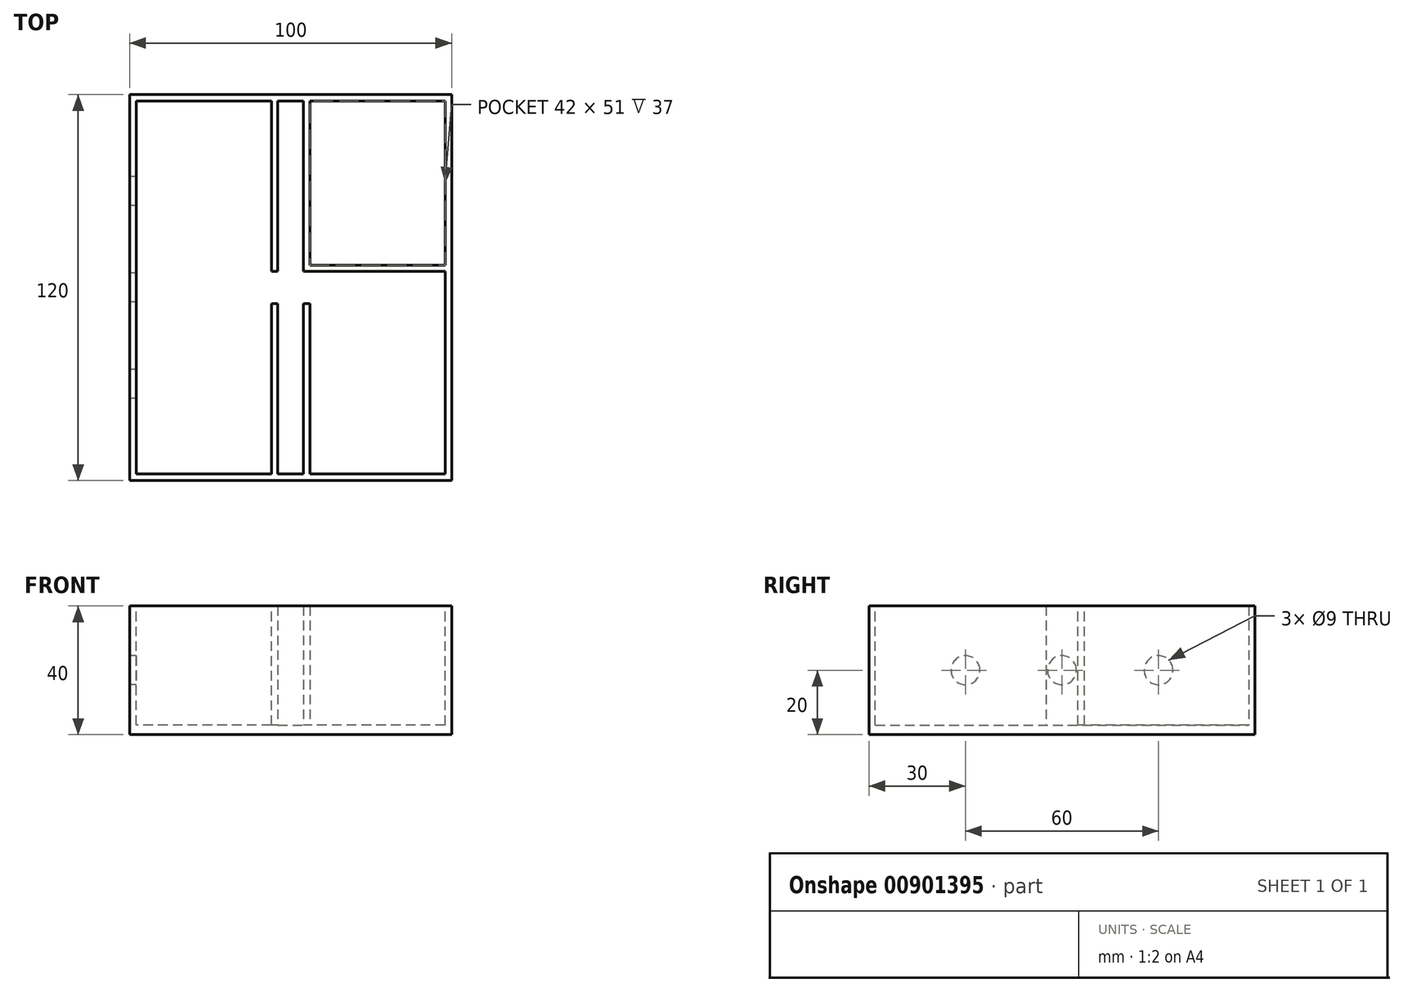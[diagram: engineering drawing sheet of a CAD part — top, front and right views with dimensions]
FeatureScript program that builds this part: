
annotation { "Feature Type Name" : "Feature", "Feature Type Description" : "" }
export const myFeature = defineFeature(function(context is Context, id is Id, definition is map)
    precondition{}
    {
        {
            var Q0;
            Q0=qCreatedBy(makeId("Top.planeOp"),FACE);
            var sketch = newSketch(context, id + "F0", { "sketchPlane" : qUnion([Q0])});
            skLineSegment(sketch, "E0.bottom", {"start": v(50, -60) * mm, "end": v(-50, -60) * mm});
            skLineSegment(sketch, "E0.top", {"start": v(50, 60) * mm, "end": v(-50, 60) * mm});
            skLineSegment(sketch, "E0.left", {"start": v(50, -60) * mm, "end": v(50, 60) * mm});
            skLineSegment(sketch, "E0.right", {"start": v(-50, -60) * mm, "end": v(-50, 60) * mm});
            skPoint(sketch, "E0.middle", {"position": v(0, 0) * mm});
            skSolve(sketch);
        }
        {
            var Q0;
            Q0=makeQuery(id+"F0.imprint","IMPRINT",FACE,{"disambiguationData":[TD([[makeQuery(id+"F0.imprint","IMPRINT",EDGE,{"derivedFrom":sQuery(id+"F0.wireOp",EDGE,"E0.bottom")}),-1.0]])]});
            extrude(context, id + "F1", {"entities" : qUnion([Q0]), "depth" : 40 * mm, "offsetDistance" : 25 * mm});
        }
        {
            var Q0;
            Q0=makeQuery(id+"F1.opExtrude","CAP_FACE",FACE,{"disambiguationData":[OSD([sQuery(id+"F0.wireOp",EDGE,"E0.bottom"),sQuery(id+"F0.wireOp",EDGE,"E0.top"),sQuery(id+"F0.wireOp",EDGE,"E0.left"),sQuery(id+"F0.wireOp",EDGE,"E0.right")])],"isStart":false});
            var sketch = newSketch(context, id + "F2", { "sketchPlane" : qUnion([Q0])});
            skLineSegment(sketch, "E1.bottom", {"start": v(48, -58) * mm, "end": v(-48, -58) * mm});
            skLineSegment(sketch, "E1.top", {"start": v(48, 58) * mm, "end": v(-48, 58) * mm});
            skLineSegment(sketch, "E1.left", {"start": v(48, -58) * mm, "end": v(48, 58) * mm});
            skLineSegment(sketch, "E1.right", {"start": v(-48, -58) * mm, "end": v(-48, 58) * mm});
            skPoint(sketch, "E1.middle", {"position": v(0, 0) * mm});
            skSolve(sketch);
        }
        {
            var Q0;
            Q0 = qSketchRegion(id + "F2", true);
            extrude(context, id + "F3", {"entities" : qUnion([Q0]), "operationType" : NewBodyOperationType.REMOVE, "oppositeDirection" : true, "depth" : 37 * mm, "offsetDistance" : 25 * mm});
        }
        {
            var Q0;
            Q0=makeQuery(id+"F1.opExtrude","SWEPT_FACE",FACE,{"disambiguationData":[OSD([sQuery(id+"F0.wireOp",EDGE,"E0.right")])]});
            var sketch = newSketch(context, id + "F4", { "sketchPlane" : qUnion([Q0])});
            skLineSegment(sketch, "E2", {"start": v(-60, 40) * mm, "end": v(60, 0) * mm, "construction": true});
            skLineSegment(sketch, "E3", {"start": v(60, 40) * mm, "end": v(-60, 0) * mm, "construction": true});
            skCircle(sketch, "E4", {"center": v(0, 20) * mm, "radius": 4.5 * mm});
            skLineSegment(sketch, "E5", {"start": v(0, 40) * mm, "end": v(-60, 0) * mm, "construction": true});
            skLineSegment(sketch, "E6", {"start": v(-60, 40) * mm, "end": v(0, 0) * mm, "construction": true});
            skLineSegment(sketch, "E7", {"start": v(0, 0) * mm, "end": v(60, 40) * mm, "construction": true});
            skLineSegment(sketch, "E8", {"start": v(60, 0) * mm, "end": v(0, 40) * mm, "construction": true});
            skCircle(sketch, "E9", {"center": v(-30, 20) * mm, "radius": 4.5 * mm});
            skCircle(sketch, "E10", {"center": v(30, 20) * mm, "radius": 4.5 * mm});
            skSolve(sketch);
        }
        {
            var Q0;
            Q0 = qSketchRegion(id + "F4", true);
            extrude(context, id + "F5", {"entities" : qUnion([Q0]), "operationType" : NewBodyOperationType.REMOVE, "oppositeDirection" : true, "depth" : 2 * mm, "offsetDistance" : 25 * mm});
        }
        {
            var Q0;
            Q0=makeQuery(id+"F3.boolean.opBoolean","COPY",FACE,{"derivedFrom":makeQuery(id+"F3.opExtrude","CAP_FACE",FACE,{"disambiguationData":[OSD([sQuery(id+"F2.wireOp",EDGE,"E1.bottom"),sQuery(id+"F2.wireOp",EDGE,"E1.top"),sQuery(id+"F2.wireOp",EDGE,"E1.left"),sQuery(id+"F2.wireOp",EDGE,"E1.right")])],"isStart":false})});
            var sketch = newSketch(context, id + "F6", { "sketchPlane" : qUnion([Q0])});
            skLineSegment(sketch, "E11", {"start": v(0, 58) * mm, "end": v(0, -58) * mm, "construction": true});
            skLineSegment(sketch, "E12", {"start": v(0, -58) * mm, "end": v(-6, -58) * mm, "construction": true});
            skLineSegment(sketch, "E13", {"start": v(0, -58) * mm, "end": v(6, -58) * mm, "construction": true});
            skLineSegment(sketch, "E14.bottom", {"start": v(-6, -58) * mm, "end": v(6, -58) * mm});
            skLineSegment(sketch, "E14.top", {"start": v(-6, 58) * mm, "end": v(6, 58) * mm});
            skLineSegment(sketch, "E14.left", {"start": v(-6, -58) * mm, "end": v(-6, 58) * mm});
            skLineSegment(sketch, "E14.right", {"start": v(6, -58) * mm, "end": v(6, 58) * mm});
            skSolve(sketch);
        }
        {
            var Q0;
            Q0 = qSketchRegion(id + "F6", true);
            extrude(context, id + "F7", {"entities" : qUnion([Q0]), "operationType" : NewBodyOperationType.ADD, "depth" : 37 * mm, "offsetDistance" : 25 * mm});
        }
        {
            var Q0;
            Q0=makeQuery(id+"F7.boolean.opBoolean","MERGE",FACE,{"derivedFrom":[makeQuery(id+"F1.opExtrude","CAP_FACE",FACE,{"disambiguationData":[OSD([sQuery(id+"F0.wireOp",EDGE,"E0.bottom"),sQuery(id+"F0.wireOp",EDGE,"E0.top"),sQuery(id+"F0.wireOp",EDGE,"E0.left"),sQuery(id+"F0.wireOp",EDGE,"E0.right")])],"isStart":false}),makeQuery(id+"F7.opExtrude","CAP_FACE",FACE,{"disambiguationData":[OSD([sQuery(id+"F6.wireOp",EDGE,"E14.bottom"),sQuery(id+"F6.wireOp",EDGE,"E14.top"),sQuery(id+"F6.wireOp",EDGE,"E14.left"),sQuery(id+"F6.wireOp",EDGE,"E14.right")])],"isStart":false})]});
            var sketch = newSketch(context, id + "F8", { "sketchPlane" : qUnion([Q0])});
            skLineSegment(sketch, "E15.bottom", {"start": v(-4, 58) * mm, "end": v(4, 58) * mm});
            skLineSegment(sketch, "E15.top", {"start": v(-4, -58) * mm, "end": v(4, -58) * mm});
            skLineSegment(sketch, "E15.left", {"start": v(-4, 58) * mm, "end": v(-4, -58) * mm});
            skLineSegment(sketch, "E15.right", {"start": v(4, 58) * mm, "end": v(4, -58) * mm});
            skSolve(sketch);
        }
        {
            var Q0;
            Q0 = qSketchRegion(id + "F8", true);
            extrude(context, id + "F9", {"entities" : qUnion([Q0]), "operationType" : NewBodyOperationType.REMOVE, "oppositeDirection" : true, "depth" : 37 * mm, "offsetDistance" : 25 * mm});
        }
        {
            var Q0;
            Q0=makeQuery(id+"F7.boolean.opBoolean","MERGE",FACE,{"derivedFrom":[makeQuery(id+"F1.opExtrude","CAP_FACE",FACE,{"disambiguationData":[OSD([sQuery(id+"F0.wireOp",EDGE,"E0.bottom"),sQuery(id+"F0.wireOp",EDGE,"E0.top"),sQuery(id+"F0.wireOp",EDGE,"E0.left"),sQuery(id+"F0.wireOp",EDGE,"E0.right")])],"isStart":false}),makeQuery(id+"F7.opExtrude","CAP_FACE",FACE,{"disambiguationData":[OSD([sQuery(id+"F6.wireOp",EDGE,"E14.bottom"),sQuery(id+"F6.wireOp",EDGE,"E14.top"),sQuery(id+"F6.wireOp",EDGE,"E14.left"),sQuery(id+"F6.wireOp",EDGE,"E14.right")])],"isStart":false})]});
            var sketch = newSketch(context, id + "F10", { "sketchPlane" : qUnion([Q0])});
            skLineSegment(sketch, "E16.bottom", {"start": v(6, -5) * mm, "end": v(-6, -5) * mm});
            skLineSegment(sketch, "E16.top", {"start": v(6, 5) * mm, "end": v(-6, 5) * mm});
            skLineSegment(sketch, "E16.left", {"start": v(6, -5) * mm, "end": v(6, 5) * mm});
            skLineSegment(sketch, "E16.right", {"start": v(-6, -5) * mm, "end": v(-6, 5) * mm});
            skPoint(sketch, "E16.middle", {"position": v(0, 0) * mm});
            skSolve(sketch);
        }
        {
            var Q0;
            Q0 = qSketchRegion(id + "F10", true);
            extrude(context, id + "F11", {"entities" : qUnion([Q0]), "operationType" : NewBodyOperationType.REMOVE, "oppositeDirection" : true, "depth" : 37 * mm, "offsetDistance" : 25 * mm});
        }
        {
            var Q0;
            Q0=makeQuery(id+"F7.boolean.opBoolean","MERGE",FACE,{"derivedFrom":[makeQuery(id+"F1.opExtrude","CAP_FACE",FACE,{"disambiguationData":[OSD([sQuery(id+"F0.wireOp",EDGE,"E0.bottom"),sQuery(id+"F0.wireOp",EDGE,"E0.top"),sQuery(id+"F0.wireOp",EDGE,"E0.left"),sQuery(id+"F0.wireOp",EDGE,"E0.right")])],"isStart":false}),makeQuery(id+"F7.opExtrude","CAP_FACE",FACE,{"disambiguationData":[OSD([sQuery(id+"F6.wireOp",EDGE,"E14.bottom"),sQuery(id+"F6.wireOp",EDGE,"E14.top"),sQuery(id+"F6.wireOp",EDGE,"E14.left"),sQuery(id+"F6.wireOp",EDGE,"E14.right")])],"isStart":false})]});
            var sketch = newSketch(context, id + "F12", { "sketchPlane" : qUnion([Q0])});
            skLineSegment(sketch, "E17.bottom", {"start": v(48, 58) * mm, "end": v(6, 58) * mm});
            skLineSegment(sketch, "E17.top", {"start": v(48, 5) * mm, "end": v(6, 5) * mm});
            skLineSegment(sketch, "E17.left", {"start": v(48, 58) * mm, "end": v(48, 5) * mm});
            skLineSegment(sketch, "E17.right", {"start": v(6, 58) * mm, "end": v(6, 5) * mm});
            skSolve(sketch);
        }
        {
            var Q0;
            Q0 = qSketchRegion(id + "F12", true);
            extrude(context, id + "F13", {"entities" : qUnion([Q0]), "operationType" : NewBodyOperationType.ADD, "depth" : -37 * mm, "offsetDistance" : 25 * mm});
        }
        {
            var Q0;
            Q0=makeQuery(id+"F13.boolean.opBoolean","MERGE",FACE,{"derivedFrom":[makeQuery(id+"F7.boolean.opBoolean","MERGE",FACE,{"derivedFrom":[makeQuery(id+"F1.opExtrude","CAP_FACE",FACE,{"disambiguationData":[OSD([sQuery(id+"F0.wireOp",EDGE,"E0.bottom"),sQuery(id+"F0.wireOp",EDGE,"E0.top"),sQuery(id+"F0.wireOp",EDGE,"E0.left"),sQuery(id+"F0.wireOp",EDGE,"E0.right")])],"isStart":false}),makeQuery(id+"F7.opExtrude","CAP_FACE",FACE,{"disambiguationData":[OSD([sQuery(id+"F6.wireOp",EDGE,"E14.bottom"),sQuery(id+"F6.wireOp",EDGE,"E14.top"),sQuery(id+"F6.wireOp",EDGE,"E14.left"),sQuery(id+"F6.wireOp",EDGE,"E14.right")])],"isStart":false})]}),makeQuery(id+"F13.opExtrude","CAP_FACE",FACE,{"disambiguationData":[OSD([sQuery(id+"F12.wireOp",EDGE,"E17.bottom"),sQuery(id+"F12.wireOp",EDGE,"E17.top"),sQuery(id+"F12.wireOp",EDGE,"E17.left"),sQuery(id+"F12.wireOp",EDGE,"E17.right")])],"isStart":true})]});
            var sketch = newSketch(context, id + "F14", { "sketchPlane" : qUnion([Q0])});
            skLineSegment(sketch, "E18.bottom", {"start": v(6, 58) * mm, "end": v(48, 58) * mm});
            skLineSegment(sketch, "E18.top", {"start": v(6, 7) * mm, "end": v(48, 7) * mm});
            skLineSegment(sketch, "E18.left", {"start": v(6, 58) * mm, "end": v(6, 7) * mm});
            skLineSegment(sketch, "E18.right", {"start": v(48, 58) * mm, "end": v(48, 7) * mm});
            skSolve(sketch);
        }
        {
            var Q0;
            Q0 = qSketchRegion(id + "F14", true);
            extrude(context, id + "F15", {"entities" : qUnion([Q0]), "operationType" : NewBodyOperationType.REMOVE, "oppositeDirection" : true, "depth" : 37 * mm, "offsetDistance" : 25 * mm});
        }
    });
